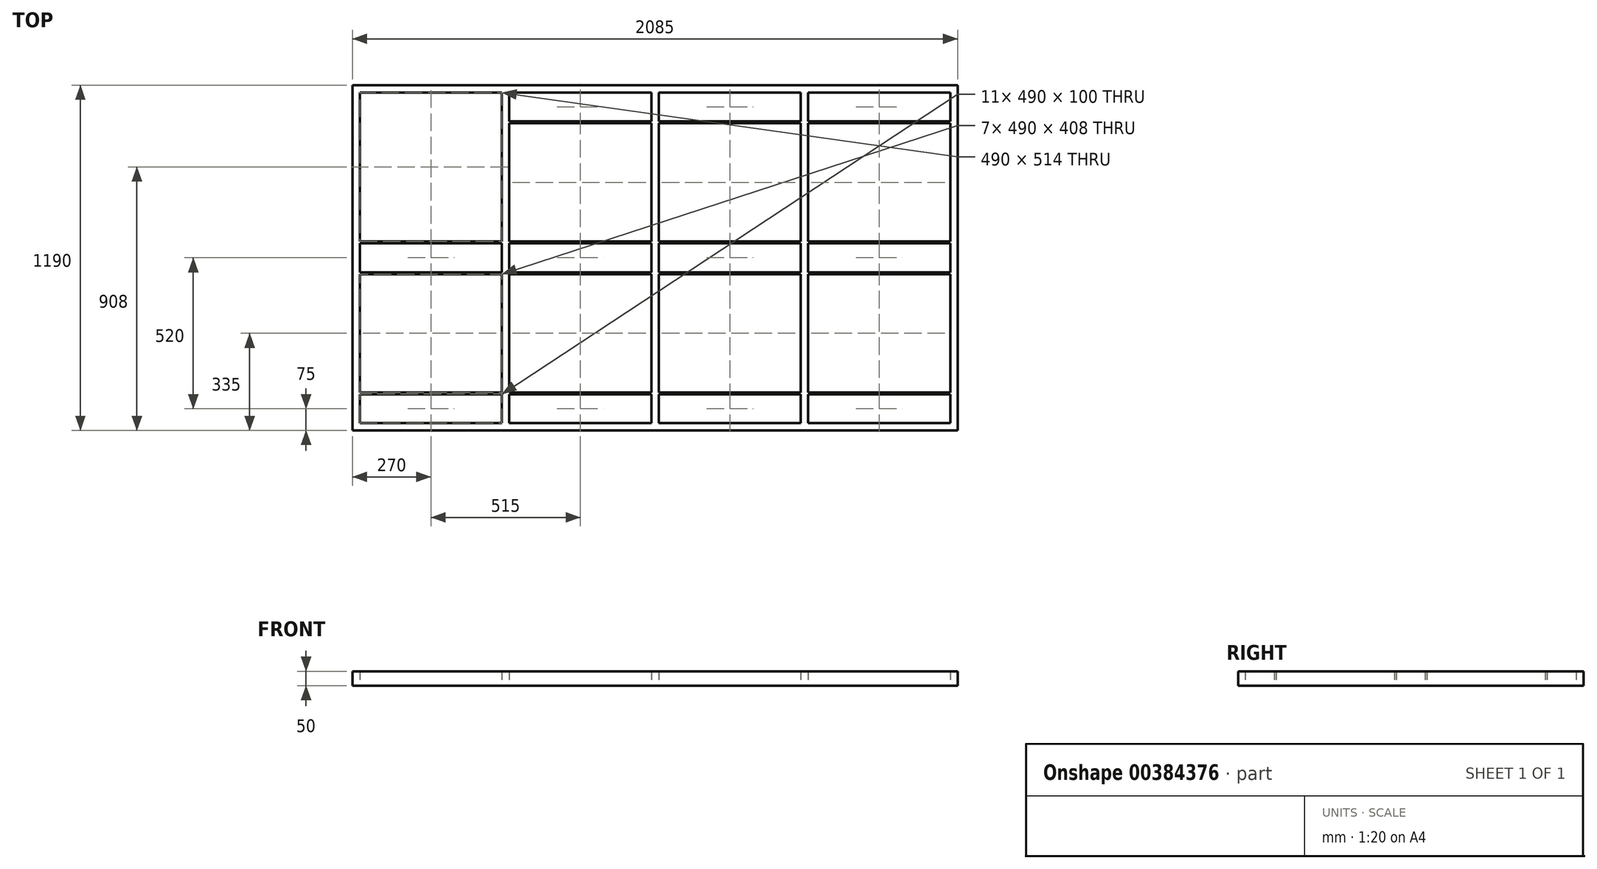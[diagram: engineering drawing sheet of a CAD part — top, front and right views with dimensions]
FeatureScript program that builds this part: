
annotation { "Feature Type Name" : "Feature", "Feature Type Description" : "" }
export const myFeature = defineFeature(function(context is Context, id is Id, definition is map)
    precondition{}
    {
        {
            var Q0;
            Q0=qCreatedBy(makeId("Top.planeOp"),FACE);
            var sketch = newSketch(context, id + "F0", { "sketchPlane" : qUnion([Q0])});
            skLineSegment(sketch, "E0.bottom", {"start": v(0, 0) * mm, "end": v(540, 0) * mm});
            skLineSegment(sketch, "E0.top", {"start": v(0, 1190) * mm, "end": v(540, 1190) * mm});
            skLineSegment(sketch, "E0.left", {"start": v(0, 0) * mm, "end": v(0, 1190) * mm});
            skLineSegment(sketch, "E0.right", {"start": v(540, 0) * mm, "end": v(540, 1190) * mm});
            skLineSegment(sketch, "E1.0", {"start": v(25, 1165) * mm, "end": v(515, 1165) * mm});
            skLineSegment(sketch, "E1.1", {"start": v(25, 25) * mm, "end": v(25, 1165) * mm});
            skLineSegment(sketch, "E1.2", {"start": v(25, 25) * mm, "end": v(515, 25) * mm});
            skLineSegment(sketch, "E1.3", {"start": v(515, 25) * mm, "end": v(515, 1165) * mm});
            skLineSegment(sketch, "E2", {"start": v(759.37, 595) * mm, "end": v(-360.82, 595) * mm, "construction": true});
            skLineSegment(sketch, "E3.bottom", {"start": v(25, 125) * mm, "end": v(515, 125) * mm});
            skLineSegment(sketch, "E3.top", {"start": v(25, 131) * mm, "end": v(515, 131) * mm});
            skLineSegment(sketch, "E3.left", {"start": v(25, 125) * mm, "end": v(25, 131) * mm});
            skLineSegment(sketch, "E3.right", {"start": v(515, 125) * mm, "end": v(515, 131) * mm});
            skLineSegment(sketch, "E4.bottom", {"start": v(25, 545) * mm, "end": v(515, 545) * mm});
            skLineSegment(sketch, "E4.top", {"start": v(25, 539) * mm, "end": v(515, 539) * mm});
            skLineSegment(sketch, "E4.left", {"start": v(25, 545) * mm, "end": v(25, 539) * mm});
            skLineSegment(sketch, "E4.right", {"start": v(515, 545) * mm, "end": v(515, 539) * mm});
            skLineSegment(sketch, "E5.MirrorCS", {"start": v(25, 645) * mm, "end": v(515, 645) * mm});
            skLineSegment(sketch, "E6.MirrorCS", {"start": v(25, 651) * mm, "end": v(515, 651) * mm});
            skLineSegment(sketch, "E7.MirrorCS", {"start": v(25, 1065) * mm, "end": v(25, 1059) * mm});
            skLineSegment(sketch, "E8.MirrorCS", {"start": v(515, 1065) * mm, "end": v(515, 1059) * mm});
            skLineSegment(sketch, "E9.MirrorCS", {"start": v(25, 1059) * mm, "end": v(515, 1059) * mm});
            skLineSegment(sketch, "E10.MirrorCS", {"start": v(25, 1065) * mm, "end": v(515, 1065) * mm});
            skLineSegment(sketch, "E11.1.0.0", {"start": v(540, 1165) * mm, "end": v(1030, 1165) * mm});
            skLineSegment(sketch, "E11.1.0.1", {"start": v(540, 1065) * mm, "end": v(1030, 1065) * mm});
            skLineSegment(sketch, "E11.1.0.2", {"start": v(515, 1190) * mm, "end": v(1055, 1190) * mm});
            skLineSegment(sketch, "E11.1.0.3", {"start": v(540, 545) * mm, "end": v(1030, 545) * mm});
            skLineSegment(sketch, "E11.1.0.4", {"start": v(540, 131) * mm, "end": v(1030, 131) * mm});
            skLineSegment(sketch, "E11.1.0.5", {"start": v(540, 651) * mm, "end": v(1030, 651) * mm});
            skLineSegment(sketch, "E11.1.0.6", {"start": v(540, 1059) * mm, "end": v(1030, 1059) * mm});
            skLineSegment(sketch, "E11.1.0.7", {"start": v(515, 0) * mm, "end": v(1055, 0) * mm});
            skLineSegment(sketch, "E11.1.0.8", {"start": v(1030, 25) * mm, "end": v(1030, 1165) * mm});
            skLineSegment(sketch, "E11.1.0.9", {"start": v(540, 539) * mm, "end": v(1030, 539) * mm});
            skLineSegment(sketch, "E11.1.0.10", {"start": v(540, 125) * mm, "end": v(1030, 125) * mm});
            skLineSegment(sketch, "E11.1.0.11", {"start": v(1274.37, 595) * mm, "end": v(154.18, 595) * mm, "construction": true});
            skLineSegment(sketch, "E11.1.0.12", {"start": v(540, 25) * mm, "end": v(1030, 25) * mm});
            skLineSegment(sketch, "E11.1.0.13", {"start": v(1055, 0) * mm, "end": v(1055, 1190) * mm});
            skLineSegment(sketch, "E11.1.0.14", {"start": v(540, 645) * mm, "end": v(1030, 645) * mm});
            skLineSegment(sketch, "E11.1.0.15", {"start": v(1030, 1065) * mm, "end": v(1030, 1059) * mm});
            skLineSegment(sketch, "E11.1.0.16", {"start": v(1030, 545) * mm, "end": v(1030, 539) * mm});
            skLineSegment(sketch, "E11.1.0.17", {"start": v(1030, 125) * mm, "end": v(1030, 131) * mm});
            skLineSegment(sketch, "E11.2.0.0", {"start": v(1055, 1165) * mm, "end": v(1545, 1165) * mm});
            skLineSegment(sketch, "E11.2.0.1", {"start": v(1055, 1065) * mm, "end": v(1545, 1065) * mm});
            skLineSegment(sketch, "E11.2.0.2", {"start": v(1030, 1190) * mm, "end": v(1570, 1190) * mm});
            skLineSegment(sketch, "E11.2.0.3", {"start": v(1055, 545) * mm, "end": v(1545, 545) * mm});
            skLineSegment(sketch, "E11.2.0.4", {"start": v(1055, 131) * mm, "end": v(1545, 131) * mm});
            skLineSegment(sketch, "E11.2.0.5", {"start": v(1055, 651) * mm, "end": v(1545, 651) * mm});
            skLineSegment(sketch, "E11.2.0.6", {"start": v(1055, 1059) * mm, "end": v(1545, 1059) * mm});
            skLineSegment(sketch, "E11.2.0.7", {"start": v(1030, 0) * mm, "end": v(1570, 0) * mm});
            skLineSegment(sketch, "E11.2.0.8", {"start": v(1545, 25) * mm, "end": v(1545, 1165) * mm});
            skLineSegment(sketch, "E11.2.0.9", {"start": v(1055, 539) * mm, "end": v(1545, 539) * mm});
            skLineSegment(sketch, "E11.2.0.10", {"start": v(1055, 125) * mm, "end": v(1545, 125) * mm});
            skLineSegment(sketch, "E11.2.0.11", {"start": v(1789.37, 595) * mm, "end": v(669.18, 595) * mm, "construction": true});
            skLineSegment(sketch, "E11.2.0.12", {"start": v(1055, 25) * mm, "end": v(1545, 25) * mm});
            skLineSegment(sketch, "E11.2.0.13", {"start": v(1570, 0) * mm, "end": v(1570, 1190) * mm});
            skLineSegment(sketch, "E11.2.0.14", {"start": v(1055, 645) * mm, "end": v(1545, 645) * mm});
            skLineSegment(sketch, "E11.2.0.15", {"start": v(1545, 1065) * mm, "end": v(1545, 1059) * mm});
            skLineSegment(sketch, "E11.2.0.16", {"start": v(1545, 545) * mm, "end": v(1545, 539) * mm});
            skLineSegment(sketch, "E11.2.0.17", {"start": v(1545, 125) * mm, "end": v(1545, 131) * mm});
            skLineSegment(sketch, "E11.direction1", {"start": v(0, 0) * mm, "end": v(515, 0) * mm, "construction": true});
            skLineSegment(sketch, "E12.0.3.0", {"start": v(1570, 1165) * mm, "end": v(2060, 1165) * mm});
            skLineSegment(sketch, "E12.3.3.0", {"start": v(1570, 1065) * mm, "end": v(2060, 1065) * mm});
            skLineSegment(sketch, "E12.6.3.0", {"start": v(1545, 1190) * mm, "end": v(2085, 1190) * mm});
            skLineSegment(sketch, "E12.9.3.0", {"start": v(1570, 545) * mm, "end": v(2060, 545) * mm});
            skLineSegment(sketch, "E12.12.3.0", {"start": v(1570, 131) * mm, "end": v(2060, 131) * mm});
            skLineSegment(sketch, "E12.15.3.0", {"start": v(1570, 651) * mm, "end": v(2060, 651) * mm});
            skLineSegment(sketch, "E12.18.3.0", {"start": v(1570, 1059) * mm, "end": v(2060, 1059) * mm});
            skLineSegment(sketch, "E12.21.3.0", {"start": v(1545, 0) * mm, "end": v(2085, 0) * mm});
            skLineSegment(sketch, "E12.24.3.0", {"start": v(2060, 25) * mm, "end": v(2060, 1165) * mm});
            skLineSegment(sketch, "E12.27.3.0", {"start": v(1570, 539) * mm, "end": v(2060, 539) * mm});
            skLineSegment(sketch, "E12.30.3.0", {"start": v(1570, 125) * mm, "end": v(2060, 125) * mm});
            skLineSegment(sketch, "E12.33.3.0", {"start": v(2304.37, 595) * mm, "end": v(1184.18, 595) * mm, "construction": true});
            skLineSegment(sketch, "E12.36.3.0", {"start": v(1570, 25) * mm, "end": v(2060, 25) * mm});
            skLineSegment(sketch, "E12.39.3.0", {"start": v(2085, 0) * mm, "end": v(2085, 1190) * mm});
            skLineSegment(sketch, "E12.42.3.0", {"start": v(1570, 645) * mm, "end": v(2060, 645) * mm});
            skLineSegment(sketch, "E12.45.3.0", {"start": v(2060, 1065) * mm, "end": v(2060, 1059) * mm});
            skLineSegment(sketch, "E12.48.3.0", {"start": v(2060, 545) * mm, "end": v(2060, 539) * mm});
            skLineSegment(sketch, "E12.51.3.0", {"start": v(2060, 125) * mm, "end": v(2060, 131) * mm});
            skSolve(sketch);
        }
        {
            var Q0;
            Q0=qSketchRegion(id+"F0",true);
            var Q1;
            Q1=makeQuery(id+"F0.imprint","IMPRINT",FACE,{"disambiguationData":[TD([[makeQuery(id+"F0.imprint","IMPRINT",EDGE,{"derivedFrom":sQuery(id+"F0.wireOp",EDGE,"E4.bottom")}),-1.0]])]});
            var Q2;
            Q2=makeQuery(id+"F0.imprint","IMPRINT",FACE,{"disambiguationData":[TD([[makeQuery(id+"F0.imprint","IMPRINT",EDGE,{"derivedFrom":sQuery(id+"F0.wireOp",EDGE,"baab227e-6a5d-40b9-91ee-7446e1ab67f20.MirrorCS")}),1.0]])]});
            var Q3;
            Q3=makeQuery(id+"F0.imprint","IMPRINT",FACE,{"disambiguationData":[TD([[makeQuery(id+"F0.imprint","IMPRINT",EDGE,{"derivedFrom":sQuery(id+"F0.wireOp",EDGE,"E3.bottom")}),1.0]])]});
            var Q4;
            Q4=makeQuery(id+"F0.imprint","IMPRINT",FACE,{"disambiguationData":[TD([[makeQuery(id+"F0.imprint","IMPRINT",EDGE,{"derivedFrom":sQuery(id+"F0.wireOp",EDGE,"TbBb99Yr-0gyQ-v6ej-gQRB-Bgt5jI2MECaT.bottom")}),-1.0]])]});
            var Q5;
            Q5=makeQuery(id+"F0.imprint","IMPRINT",FACE,{"disambiguationData":[TD([[makeQuery(id+"F0.imprint","IMPRINT",EDGE,{"derivedFrom":sQuery(id+"F0.wireOp",EDGE,"NzViuoU3-R4T5-xjC5-rI0y-QMhb7gm5c65x.bottom")}),-1.0]])]});
            var Q6;
            Q6=makeQuery(id+"F0.imprint","IMPRINT",FACE,{"disambiguationData":[TD([[makeQuery(id+"F0.imprint","IMPRINT",EDGE,{"derivedFrom":sQuery(id+"F0.wireOp",EDGE,"baab227e-6a5d-40b9-91ee-7446e1ab67f23.MirrorCS")}),-1.0]])]});
            var Q7;
            Q7=makeQuery(id+"F0.imprint","IMPRINT",FACE,{"disambiguationData":[TD([[makeQuery(id+"F0.imprint","IMPRINT",EDGE,{"derivedFrom":sQuery(id+"F0.wireOp",EDGE,"baab227e-6a5d-40b9-91ee-7446e1ab67f22.MirrorCS")}),-1.0]])]});
            var Q8;
            Q8=makeQuery(id+"F0.imprint","IMPRINT",FACE,{"disambiguationData":[TD([[makeQuery(id+"F0.imprint","IMPRINT",EDGE,{"derivedFrom":sQuery(id+"F0.wireOp",EDGE,"baab227e-6a5d-40b9-91ee-7446e1ab67f21.MirrorCS")}),1.0]])]});
            var Q9;
            {var subQ0=sQuery(id+"F0.wireOp",EDGE,"E5.MirrorCS");Q9=makeQuery(id+"F0.imprint","IMPRINT",FACE,{"disambiguationData":[TD([[makeQuery(id+"F0.imprint","IMPRINT",EDGE,{"derivedFrom":subQ0}),1.0]])]});}
            var Q10;
            Q10=makeQuery(id+"F0.imprint","IMPRINT",FACE,{"disambiguationData":[TD([[makeQuery(id+"F0.imprint","IMPRINT",EDGE,{"derivedFrom":sQuery(id+"F0.wireOp",EDGE,"E7.MirrorCS")}),1.0]])]});
            var Q11;
            {var subQ0=sQuery(id+"F0.wireOp",EDGE,"E11.1.0.5");Q11=makeQuery(id+"F0.imprint","IMPRINT",FACE,{"disambiguationData":[TD([[makeQuery(id+"F0.imprint","IMPRINT",EDGE,{"derivedFrom":subQ0}),-1.0]])]});}
            var Q12;
            {var subQ0=sQuery(id+"F0.wireOp",EDGE,"E11.2.0.5");Q12=makeQuery(id+"F0.imprint","IMPRINT",FACE,{"disambiguationData":[TD([[makeQuery(id+"F0.imprint","IMPRINT",EDGE,{"derivedFrom":subQ0}),-1.0]])]});}
            var Q13;
            {var subQ0=sQuery(id+"F0.wireOp",EDGE,"E11.2.0.3");Q13=makeQuery(id+"F0.imprint","IMPRINT",FACE,{"disambiguationData":[TD([[makeQuery(id+"F0.imprint","IMPRINT",EDGE,{"derivedFrom":subQ0}),-1.0]])]});}
            var Q14;
            {var subQ0=sQuery(id+"F0.wireOp",EDGE,"E11.1.0.3");Q14=makeQuery(id+"F0.imprint","IMPRINT",FACE,{"disambiguationData":[TD([[makeQuery(id+"F0.imprint","IMPRINT",EDGE,{"derivedFrom":subQ0}),-1.0]])]});}
            var Q15;
            {var subQ0=sQuery(id+"F0.wireOp",EDGE,"E12.9.3.0");Q15=makeQuery(id+"F0.imprint","IMPRINT",FACE,{"disambiguationData":[TD([[makeQuery(id+"F0.imprint","IMPRINT",EDGE,{"derivedFrom":subQ0}),-1.0]])]});}
            var Q16;
            {var subQ0=sQuery(id+"F0.wireOp",EDGE,"E12.15.3.0");Q16=makeQuery(id+"F0.imprint","IMPRINT",FACE,{"disambiguationData":[TD([[makeQuery(id+"F0.imprint","IMPRINT",EDGE,{"derivedFrom":subQ0}),-1.0]])]});}
            var Q17;
            {var subQ0=sQuery(id+"F0.wireOp",EDGE,"E12.3.3.0");Q17=makeQuery(id+"F0.imprint","IMPRINT",FACE,{"disambiguationData":[TD([[makeQuery(id+"F0.imprint","IMPRINT",EDGE,{"derivedFrom":subQ0}),-1.0]])]});}
            var Q18;
            {var subQ0=sQuery(id+"F0.wireOp",EDGE,"E11.2.0.1");Q18=makeQuery(id+"F0.imprint","IMPRINT",FACE,{"disambiguationData":[TD([[makeQuery(id+"F0.imprint","IMPRINT",EDGE,{"derivedFrom":subQ0}),-1.0]])]});}
            var Q19;
            {var subQ0=sQuery(id+"F0.wireOp",EDGE,"E11.1.0.1");Q19=makeQuery(id+"F0.imprint","IMPRINT",FACE,{"disambiguationData":[TD([[makeQuery(id+"F0.imprint","IMPRINT",EDGE,{"derivedFrom":subQ0}),-1.0]])]});}
            var Q20;
            {var subQ0=sQuery(id+"F0.wireOp",EDGE,"E12.12.3.0");Q20=makeQuery(id+"F0.imprint","IMPRINT",FACE,{"disambiguationData":[TD([[makeQuery(id+"F0.imprint","IMPRINT",EDGE,{"derivedFrom":subQ0}),-1.0]])]});}
            var Q21;
            {var subQ0=sQuery(id+"F0.wireOp",EDGE,"E11.1.0.4");Q21=makeQuery(id+"F0.imprint","IMPRINT",FACE,{"disambiguationData":[TD([[makeQuery(id+"F0.imprint","IMPRINT",EDGE,{"derivedFrom":subQ0}),-1.0]])]});}
            var Q22;
            {var subQ0=sQuery(id+"F0.wireOp",EDGE,"E11.2.0.4");Q22=makeQuery(id+"F0.imprint","IMPRINT",FACE,{"disambiguationData":[TD([[makeQuery(id+"F0.imprint","IMPRINT",EDGE,{"derivedFrom":subQ0}),-1.0]])]});}
            extrude(context, id + "F1", {"entities" : qUnion([Q0, Q1, Q2, Q3, Q4, Q5, Q6, Q7, Q8, Q9, Q10, Q11, Q12, Q13, Q14, Q15, Q16, Q17, Q18, Q19, Q20, Q21, Q22]), "depth" : 50 * mm});
        }
        {
            var Q0;
            Q0=makeQuery(id+"F1.opExtrude","SWEPT_FACE",FACE,{"disambiguationData":[OSD([sQuery(id+"F0.wireOp",EDGE,"E3.top")])]});
            var sketch = newSketch(context, id + "F2", { "sketchPlane" : qUnion([Q0])});
            skLineSegment(sketch, "E13", {"start": v(-265, -37.36) * mm, "end": v(-265, 103.2) * mm, "construction": true});
            skPoint(sketch, "E13.startSnap0", {"position": v(-265, 25) * mm});
            skCircle(sketch, "E14", {"center": v(-265, 25) * mm, "radius": 9.5 * mm});
            skLineSegment(sketch, "E15", {"start": v(-25, 25) * mm, "end": v(-265, 25) * mm, "construction": true});
            skLineSegment(sketch, "E16", {"start": v(-515, 25) * mm, "end": v(-265, 25) * mm, "construction": true});
            skCircle(sketch, "E17", {"center": v(-145, 25) * mm, "radius": 9.5 * mm});
            skCircle(sketch, "E18", {"center": v(-390, 25) * mm, "radius": 9.5 * mm});
            skLineSegment(sketch, "E19", {"start": v(-527.5, -35.14) * mm, "end": v(-527.5, 158.1) * mm, "construction": true});
            skCircle(sketch, "E20.MirrorC", {"center": v(-790, 25) * mm, "radius": 9.5 * mm});
            skCircle(sketch, "E21.MirrorC", {"center": v(-910, 25) * mm, "radius": 9.5 * mm});
            skCircle(sketch, "E22.MirrorC", {"center": v(-665, 25) * mm, "radius": 9.5 * mm});
            skLineSegment(sketch, "E23", {"start": v(-1042.5, -68.6) * mm, "end": v(-1042.5, 150.41) * mm, "construction": true});
            skCircle(sketch, "E24.MirrorC", {"center": v(-1820, 25) * mm, "radius": 9.5 * mm});
            skCircle(sketch, "E25.MirrorC", {"center": v(-1295, 25) * mm, "radius": 9.5 * mm});
            skCircle(sketch, "E26.MirrorC", {"center": v(-1695, 25) * mm, "radius": 9.5 * mm});
            skCircle(sketch, "E27.MirrorC", {"center": v(-1175, 25) * mm, "radius": 9.5 * mm});
            skCircle(sketch, "E28.MirrorC", {"center": v(-1940, 25) * mm, "radius": 9.5 * mm});
            skCircle(sketch, "E29.MirrorC", {"center": v(-1420, 25) * mm, "radius": 9.5 * mm});
            skSolve(sketch);
        }
        {
            var Q0;
            Q0=sQuery(id+"F2.wireOp",EDGE,"E17");
            var Q1;
            Q1=sQuery(id+"F2.wireOp",EDGE,"E14");
            var Q2;
            Q2=sQuery(id+"F2.wireOp",EDGE,"E18");
            var Q3;
            Q3=sQuery(id+"F2.wireOp",EDGE,"E22.MirrorC");
            var Q4;
            Q4=sQuery(id+"F2.wireOp",EDGE,"E20.MirrorC");
            var Q5;
            Q5=sQuery(id+"F2.wireOp",EDGE,"E21.MirrorC");
            var Q6;
            Q6=sQuery(id+"F2.wireOp",EDGE,"E27.MirrorC");
            var Q7;
            Q7=sQuery(id+"F2.wireOp",EDGE,"E25.MirrorC");
            var Q8;
            Q8=sQuery(id+"F2.wireOp",EDGE,"E29.MirrorC");
            var Q9;
            Q9=sQuery(id+"F2.wireOp",EDGE,"E26.MirrorC");
            var Q10;
            Q10=sQuery(id+"F2.wireOp",EDGE,"E24.MirrorC");
            var Q11;
            Q11=sQuery(id+"F2.wireOp",EDGE,"E28.MirrorC");
            extrude(context, id + "F3", {"bodyType" : ToolBodyType.SURFACE, "surfaceEntities" : qUnion([Q0, Q1, Q2, Q3, Q4, Q5, Q6, Q7, Q8, Q9, Q10, Q11]), "endBound" : BoundingType.UP_TO_NEXT, "depth" : 25 * mm});
        }
        {
            var Q0;
            Q0=makeQuery(id+"F1.opExtrude","SWEPT_FACE",FACE,{"disambiguationData":[OSD([sQuery(id+"F0.wireOp",EDGE,"E6.MirrorCS")])]});
            var sketch = newSketch(context, id + "F4", { "sketchPlane" : qUnion([Q0])});
            skLineSegment(sketch, "E30", {"start": v(-515, 25) * mm, "end": v(-270, 25) * mm, "construction": true});
            skLineSegment(sketch, "E31", {"start": v(-270, 25) * mm, "end": v(-25, 25) * mm, "construction": true});
            skCircle(sketch, "E32", {"center": v(-392.5, 25) * mm, "radius": 9.5 * mm});
            skCircle(sketch, "E33", {"center": v(-270, 25) * mm, "radius": 9.5 * mm});
            skCircle(sketch, "E34", {"center": v(-147.5, 25) * mm, "radius": 9.5 * mm});
            skLineSegment(sketch, "E35", {"start": v(-540, 25) * mm, "end": v(-1030, 25) * mm, "construction": true});
            skLineSegment(sketch, "E36", {"start": v(-527.5, 96.55) * mm, "end": v(-527.5, -41.55) * mm, "construction": true});
            skLineSegment(sketch, "E37", {"start": v(-1042.5, -33.14) * mm, "end": v(-1042.5, 110.96) * mm, "construction": true});
            skCircle(sketch, "E38.MirrorC", {"center": v(-662.5, 25) * mm, "radius": 9.5 * mm});
            skCircle(sketch, "E39.MirrorC", {"center": v(-785, 25) * mm, "radius": 9.5 * mm});
            skCircle(sketch, "E40.MirrorC", {"center": v(-907.5, 25) * mm, "radius": 9.5 * mm});
            skCircle(sketch, "E41.MirrorC", {"center": v(-1177.5, 25) * mm, "radius": 9.5 * mm});
            skCircle(sketch, "E42.MirrorC", {"center": v(-1300, 25) * mm, "radius": 9.5 * mm});
            skCircle(sketch, "E43.MirrorC", {"center": v(-1422.5, 25) * mm, "radius": 9.5 * mm});
            skCircle(sketch, "E44.MirrorC", {"center": v(-1692.5, 25) * mm, "radius": 9.5 * mm});
            skCircle(sketch, "E45.MirrorC", {"center": v(-1815, 25) * mm, "radius": 9.5 * mm});
            skCircle(sketch, "E46.MirrorC", {"center": v(-1937.5, 25) * mm, "radius": 9.5 * mm});
            skSolve(sketch);
        }
        {
            var Q0;
            Q0=sQuery(id+"F4.wireOp",EDGE,"E34");
            var Q1;
            Q1=sQuery(id+"F4.wireOp",EDGE,"E33");
            var Q2;
            Q2=sQuery(id+"F4.wireOp",EDGE,"E32");
            var Q3;
            Q3=sQuery(id+"F4.wireOp",EDGE,"E38.MirrorC");
            var Q4;
            Q4=sQuery(id+"F4.wireOp",EDGE,"E39.MirrorC");
            var Q5;
            Q5=sQuery(id+"F4.wireOp",EDGE,"E40.MirrorC");
            var Q6;
            Q6=sQuery(id+"F4.wireOp",EDGE,"E41.MirrorC");
            var Q7;
            Q7=sQuery(id+"F4.wireOp",EDGE,"E42.MirrorC");
            var Q8;
            Q8=sQuery(id+"F4.wireOp",EDGE,"E43.MirrorC");
            var Q9;
            Q9=sQuery(id+"F4.wireOp",EDGE,"E44.MirrorC");
            var Q10;
            Q10=sQuery(id+"F4.wireOp",EDGE,"E45.MirrorC");
            var Q11;
            Q11=sQuery(id+"F4.wireOp",EDGE,"E46.MirrorC");
            extrude(context, id + "F5", {"bodyType" : ToolBodyType.SURFACE, "surfaceEntities" : qUnion([Q0, Q1, Q2, Q3, Q4, Q5, Q6, Q7, Q8, Q9, Q10, Q11]), "endBound" : BoundingType.UP_TO_NEXT, "depth" : 25 * mm});
        }
    });
